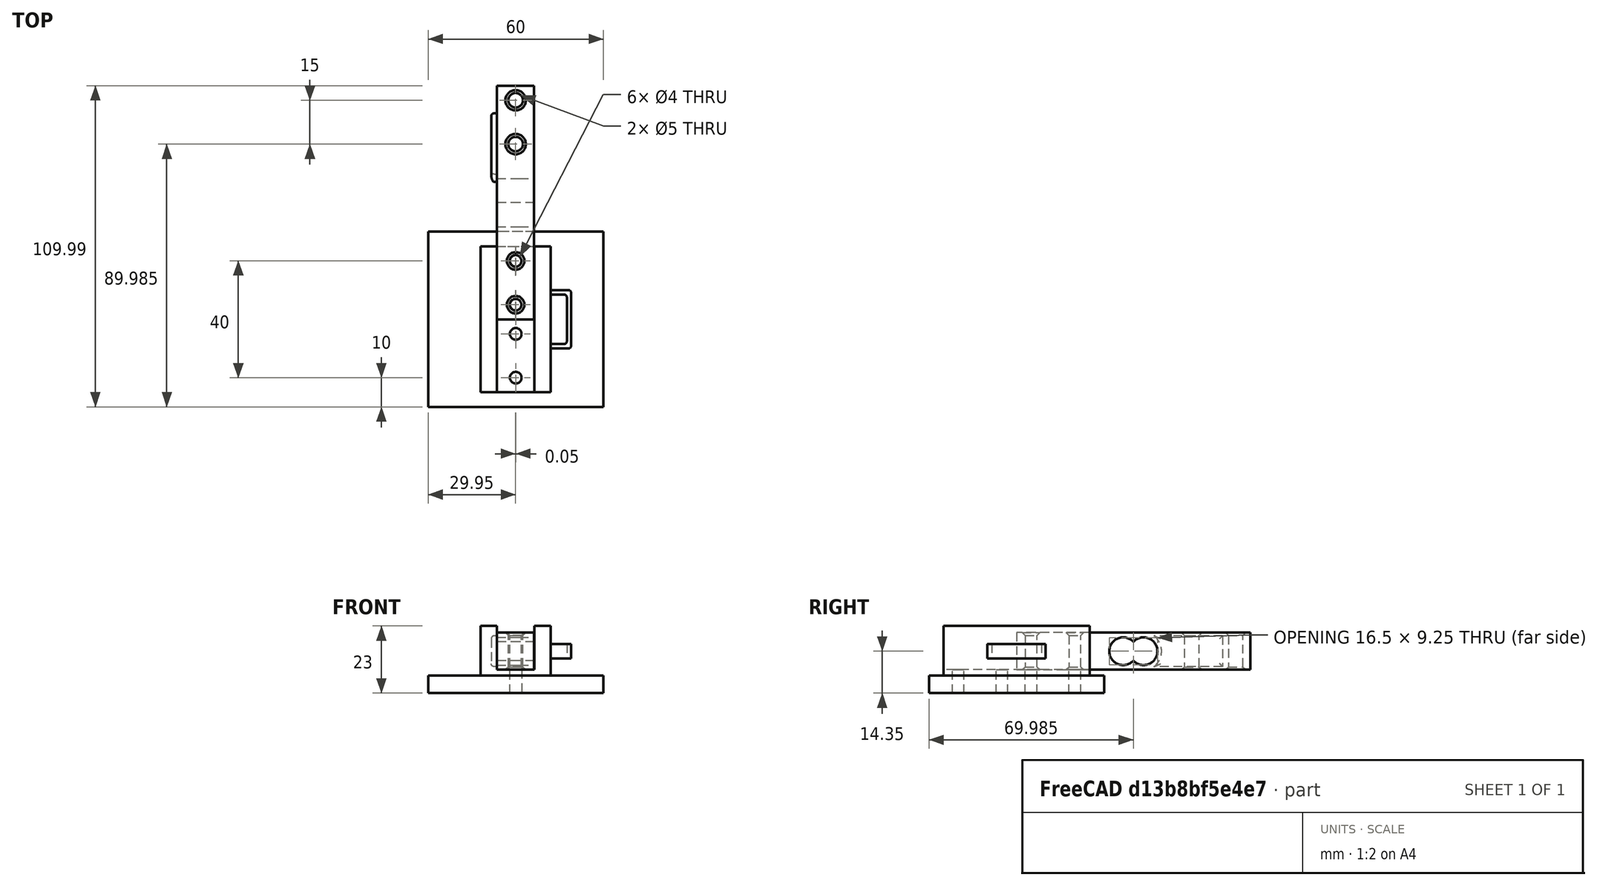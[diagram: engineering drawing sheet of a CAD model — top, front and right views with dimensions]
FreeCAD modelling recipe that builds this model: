
FCSTD DOCUMENT  (FreeCAD 0.19R24267 +148 (Git))
Label: assembly_V2
License: All rights reserved
LicenseURL: http://en.wikipedia.org/wiki/All_rights_reserved
objects: App::FeaturePython×8, Part::FeaturePython×2, PartDesign::FeatureBase×1, PartDesign::Body×1
note: 4 computed .brp shape members not serialized (recipe doc carries the construction recipe); baked Part::Feature solids carry a one-line shape summary decoded from their .brp

FEATURE [Part::FeaturePython] b__xd0_xb4_xd0_xb5_xd1_x80_xd0_xb6_xd0_xb0_xd1_x82_xd0_xb5_xd0_xbb_xd1_x8c_V2_001_  label="держатель_V2_001"  # a2plus imported part (geometry in sourceFile) (typed FeaturePython)
  a2p_Version = V0.1
  fixedPosition = true
  objectType = a2pPart
  sourceFile = .\держатель_V2.FCStd
  subassemblyImport = false
  timeLastImport = 1.6528e+09
  updateColors = true
FEATURE [Part::FeaturePython] b__xd1_x82_xd0_xb5_xd0_xbd_xd0_xb7_xd0_xbe_xd0_xb4_xd0_xb0_xd1_x82_xd1_x87_xd0_xb8_xd0_xba__xd0_xbc_xd0_xbe_xd0_xb4_xd0_xb5_xd0_xbb_xd1_x8c_001_  label="тензодатчик модель_001"  # a2plus imported part (geometry in sourceFile) (typed FeaturePython)
  Placement = pos=(36.3,29.9854,8) rot=(0.57735,-0.57735,-0.57735;2.0944rad)
  a2p_Version = V0.1
  fixedPosition = false
  objectType = a2pPart
  sourceFile = .\тензодатчик модель.FCStd
  subassemblyImport = false
  timeLastImport = 1.65275e+09
  updateColors = true
FEATURE [App::FeaturePython] planeCoincident_001  label="planeCoincident_001__тензодатчик модель_001"  # a2plus constraint (typed FeaturePython)
  Object1 = b__xd0_xb4_xd0_xb5_xd1_x80_xd0_xb6_xd0_xb0_xd1_x82_xd0_xb5_xd0_xbb_xd1_x8c_V2_001_
  Object2 = b__xd1_x82_xd0_xb5_xd0_xbd_xd0_xb7_xd0_xbe_xd0_xb4_xd0_xb0_xd1_x82_xd1_x87_xd0_xb8_xd0_xba__xd0_xbc_xd0_xbe_xd0_xb4_xd0_xb5_xd0_xbb_xd1_x8c_001_
  ParentTreeObject = -> b__xd0_xb4_xd0_xb5_xd1_x80_xd0_xb6_xd0_xb0_xd1_x82_xd0_xb5_xd0_xbb_xd1_x8c_V2_001_
  SubElement1 = Face23
  SubElement2 = Face10
  Suppressed = false
  Type = plane
  directionConstraint = 1
  offset = 0
FEATURE [App::FeaturePython] planeCoincident_001_mirror  label="planeCoincident_001__держатель_V2_001"  # a2plus constraint (typed FeaturePython)
  Object1 = b__xd0_xb4_xd0_xb5_xd1_x80_xd0_xb6_xd0_xb0_xd1_x82_xd0_xb5_xd0_xbb_xd1_x8c_V2_001_
  Object2 = b__xd1_x82_xd0_xb5_xd0_xbd_xd0_xb7_xd0_xbe_xd0_xb4_xd0_xb0_xd1_x82_xd1_x87_xd0_xb8_xd0_xba__xd0_xbc_xd0_xbe_xd0_xb4_xd0_xb5_xd0_xbb_xd1_x8c_001_
  ParentTreeObject = -> b__xd1_x82_xd0_xb5_xd0_xbd_xd0_xb7_xd0_xbe_xd0_xb4_xd0_xb0_xd1_x82_xd1_x87_xd0_xb8_xd0_xba__xd0_xbc_xd0_xbe_xd0_xb4_xd0_xb5_xd0_xbb_xd1_x8c_001_
  SubElement1 = Face23
  SubElement2 = Face10
  Suppressed = false
  Type = plane
  directionConstraint = 1
  offset = 0
FEATURE [PartDesign::FeatureBase] Clone
  BaseFeature = -> b__xd1_x82_xd0_xb5_xd0_xbd_xd0_xb7_xd0_xbe_xd0_xb4_xd0_xb0_xd1_x82_xd1_x87_xd0_xb8_xd0_xba__xd0_xbc_xd0_xbe_xd0_xb4_xd0_xb5_xd0_xbb_xd1_x8c_001_
  Placement = pos=(23.6,29.9854,8) rot=(0.57735,0.57735,0.57735;2.0944rad)
FEATURE [PartDesign::Body] Body  label="тензодатчик модель_002"
  BaseFeature = -> b__xd1_x82_xd0_xb5_xd0_xbd_xd0_xb7_xd0_xbe_xd0_xb4_xd0_xb0_xd1_x82_xd1_x87_xd0_xb8_xd0_xba__xd0_xbc_xd0_xbe_xd0_xb4_xd0_xb5_xd0_xbb_xd1_x8c_001_
  Group = -> [Clone]
  Origin = -> Origin
  Tip = -> Clone
FEATURE [App::FeaturePython] planeCoincident_002  label="planeCoincident_002__Clone"  # a2plus constraint (typed FeaturePython)
  Object1 = b__xd0_xb4_xd0_xb5_xd1_x80_xd0_xb6_xd0_xb0_xd1_x82_xd0_xb5_xd0_xbb_xd1_x8c_V2_001_
  Object2 = Clone
  ParentTreeObject = -> b__xd0_xb4_xd0_xb5_xd1_x80_xd0_xb6_xd0_xb0_xd1_x82_xd0_xb5_xd0_xbb_xd1_x8c_V2_001_
  SubElement1 = Face23
  SubElement2 = Face10
  Suppressed = false
  Type = plane
  directionConstraint = 1
  offset = 0
FEATURE [App::FeaturePython] planeCoincident_002_mirror  label="planeCoincident_002__держатель_V2_001"  # a2plus constraint (typed FeaturePython)
  Object1 = b__xd0_xb4_xd0_xb5_xd1_x80_xd0_xb6_xd0_xb0_xd1_x82_xd0_xb5_xd0_xbb_xd1_x8c_V2_001_
  Object2 = Clone
  ParentTreeObject = -> Clone
  SubElement1 = Face23
  SubElement2 = Face10
  Suppressed = false
  Type = plane
  directionConstraint = 1
  offset = 0
FEATURE [App::FeaturePython] planeCoincident_003  label="planeCoincident_003__держатель_V2_001"  # a2plus constraint (typed FeaturePython)
  Object1 = b__xd1_x82_xd0_xb5_xd0_xbd_xd0_xb7_xd0_xbe_xd0_xb4_xd0_xb0_xd1_x82_xd1_x87_xd0_xb8_xd0_xba__xd0_xbc_xd0_xbe_xd0_xb4_xd0_xb5_xd0_xbb_xd1_x8c_001_
  Object2 = b__xd0_xb4_xd0_xb5_xd1_x80_xd0_xb6_xd0_xb0_xd1_x82_xd0_xb5_xd0_xbb_xd1_x8c_V2_001_
  ParentTreeObject = -> b__xd1_x82_xd0_xb5_xd0_xbd_xd0_xb7_xd0_xbe_xd0_xb4_xd0_xb0_xd1_x82_xd1_x87_xd0_xb8_xd0_xba__xd0_xbc_xd0_xbe_xd0_xb4_xd0_xb5_xd0_xbb_xd1_x8c_001_
  SubElement1 = Face21
  SubElement2 = Face31
  Suppressed = false
  Type = plane
  directionConstraint = 1
  offset = 0
FEATURE [App::FeaturePython] planeCoincident_003_mirror  label="planeCoincident_003__тензодатчик модель_001"  # a2plus constraint (typed FeaturePython)
  Object1 = b__xd1_x82_xd0_xb5_xd0_xbd_xd0_xb7_xd0_xbe_xd0_xb4_xd0_xb0_xd1_x82_xd1_x87_xd0_xb8_xd0_xba__xd0_xbc_xd0_xbe_xd0_xb4_xd0_xb5_xd0_xbb_xd1_x8c_001_
  Object2 = b__xd0_xb4_xd0_xb5_xd1_x80_xd0_xb6_xd0_xb0_xd1_x82_xd0_xb5_xd0_xbb_xd1_x8c_V2_001_
  ParentTreeObject = -> b__xd0_xb4_xd0_xb5_xd1_x80_xd0_xb6_xd0_xb0_xd1_x82_xd0_xb5_xd0_xbb_xd1_x8c_V2_001_
  SubElement1 = Face21
  SubElement2 = Face31
  Suppressed = false
  Type = plane
  directionConstraint = 1
  offset = 0
FEATURE [App::FeaturePython] planeCoincident_004  label="planeCoincident_004__держатель_V2_001"  # a2plus constraint (typed FeaturePython)
  Object1 = Clone
  Object2 = b__xd0_xb4_xd0_xb5_xd1_x80_xd0_xb6_xd0_xb0_xd1_x82_xd0_xb5_xd0_xbb_xd1_x8c_V2_001_
  ParentTreeObject = -> Clone
  SubElement1 = Face4
  SubElement2 = Face31
  Suppressed = false
  Type = plane
  directionConstraint = 0
  offset = 0
FEATURE [App::FeaturePython] planeCoincident_004_mirror  label="planeCoincident_004__Clone"  # a2plus constraint (typed FeaturePython)
  Object1 = Clone
  Object2 = b__xd0_xb4_xd0_xb5_xd1_x80_xd0_xb6_xd0_xb0_xd1_x82_xd0_xb5_xd0_xbb_xd1_x8c_V2_001_
  ParentTreeObject = -> b__xd0_xb4_xd0_xb5_xd1_x80_xd0_xb6_xd0_xb0_xd1_x82_xd0_xb5_xd0_xbb_xd1_x8c_V2_001_
  SubElement1 = Face4
  SubElement2 = Face31
  Suppressed = false
  Type = plane
  directionConstraint = 0
  offset = 0
